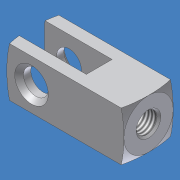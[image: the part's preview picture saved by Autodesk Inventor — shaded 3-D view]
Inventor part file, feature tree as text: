
AUTODESK INVENTOR PART (.ipt)
format: ipt  version: 2012 (Build 160160000, 160)  size: 169,472 bytes
history: native  units: mm (DEFAULTED — no unit token found)
features: other x126, sketch x7, revolve x5, extrude x2, thread x1
ambient origin geometry x8: Origin, YZ Plane, XZ Plane, XY Plane, X Axis, Y Axis, Z Axis, Center Point
bodies: Solid1 (feature_tree)
feature tree (141):
  extrude  "Extrusion1"  Depth=12.7mm TaperAngle=0.0deg
  extrude  "Extrusion2"  Depth=10.68451mm TaperAngle=0.0deg
  revolve  "Revolution1"  Angle=360.0deg
  thread  "Thread1"  [1 undecoded]
  revolve  "Revolution2"  [1 undecoded]
  revolve  "Revolution3"  [1 undecoded]
  revolve  "Revolution4"  [1 undecoded]
  revolve  "Revolution5"  [1 undecoded]
  other  "th1_XY"
  other  "th1_YZ"
  other  "th1_ZX"
  other  "th1_X"
  other  "th1_Y"
  other  "th1_Z"
  other  "th1_Center"
  other  "th2_XY"
  other  "th2_YZ"
  other  "th2_ZX"
  other  "th2_X"
  other  "th2_Y"
  other  "th2_Z"
  other  "th2_Center"
  other  "rod_clevis_body_XY"
  other  "rod_clevis_body_YZ"
  other  "rod_clevis_body_ZX"
  other  "rod_clevis_body_X"
  other  "rod_clevis_body_Y"
  other  "rod_clevis_body_Z"
  other  "rod_clevis_body_Center"
  other  "piston_rod_clevis_XY"
  other  "piston_rod_clevis_YZ"
  other  "piston_rod_clevis_ZX"
  other  "piston_rod_clevis_X"
  other  "piston_rod_clevis_Y"
  other  "piston_rod_clevis_Z"
  other  "piston_rod_clevis_Center"
  other  "dummy_XY"
  other  "dummy_YZ"
  other  "dummy_ZX"
  other  "dummy_X"
  other  "dummy_Y"
  other  "dummy_Z"
  other  "dummy_Center"
  other  "l11_XY"
  other  "l11_YZ"
  other  "l11_ZX"
  other  "l11_X"
  other  "l11_Y"
  other  "l11_Z"
  other  "l11_Center"
  other  "l12_XY"
  other  "l12_YZ"
  other  "l12_ZX"
  other  "l12_X"
  other  "l12_Y"
  other  "l12_Z"
  other  "l12_Center"
  other  "l1_XY"
  other  "l1_YZ"
  other  "l1_ZX"
  other  "l1_X"
  other  "l1_Y"
  other  "l1_Z"
  other  "l1_Center"
  other  "h1_XY"
  other  "h1_YZ"
  other  "h1_ZX"
  other  "h1_X"
  other  "h1_Y"
  other  "h1_Z"
  other  "h1_Center"
  other  "l2_XY"
  other  "l2_YZ"
  other  "l2_ZX"
  other  "l2_X"
  other  "l2_Y"
  other  "l2_Z"
  other  "l2_Center"
  other  "h2_XY"
  other  "h2_YZ"
  other  "h2_ZX"
  other  "h2_X"
  other  "h2_Y"
  other  "h2_Z"
  other  "h2_Center"
  other  "w11_XY"
  other  "w11_YZ"
  other  "w11_ZX"
  other  "w11_X"
  other  "w11_Y"
  other  "w11_Z"
  other  "w11_Center"
  other  "w12_XY"
  other  "w12_YZ"
  other  "w12_ZX"
  other  "w12_X"
  other  "w12_Y"
  other  "w12_Z"
  other  "w12_Center"
  other  "l21_XY"
  other  "l21_YZ"
  other  "l21_ZX"
  other  "l21_X"
  other  "l21_Y"
  other  "l21_Z"
  other  "l21_Center"
  other  "l22_XY"
  other  "l22_YZ"
  other  "l22_ZX"
  other  "l22_X"
  other  "l22_Y"
  other  "l22_Z"
  other  "l22_Center"
  other  "w1_XY"
  other  "w1_YZ"
  other  "w1_ZX"
  other  "w1_X"
  other  "w1_Y"
  other  "w1_Z"
  other  "w1_Center"
  other  "w2_XY"
  other  "w2_YZ"
  other  "w2_ZX"
  other  "w2_X"
  other  "w2_Y"
  other  "w2_Z"
  other  "w2_Center"
  other  "to_cylinder_XY"
  other  "to_cylinder_YZ"
  other  "to_cylinder_ZX"
  other  "to_cylinder_X"
  other  "to_cylinder_Y"
  other  "to_cylinder_Z"
  other  "to_cylinder_Center"
  sketch  "Sketch_1"  dims[d0=12.7mm d1=0.0mm d2=12.7mm d3=0.0mm]
  sketch  "Sketch_2"  dims[d4=360.0deg d5=10.68451mm d6=0.0mm]
  sketch  "Sketch_3"  dims[d7=360.0deg d8=360.0deg d9=360.0deg]
  sketch  "Sketch_4"  dims[d10=360.0deg]
  sketch  "Sketch_5"
  sketch  "Sketch_9"
  sketch  "Sketch_10"
note: 5 required parameter values undecoded (feature->parameter linkage not recoverable at this tier; creation-order binding heuristic only, values carry confidence <= 0.55)
